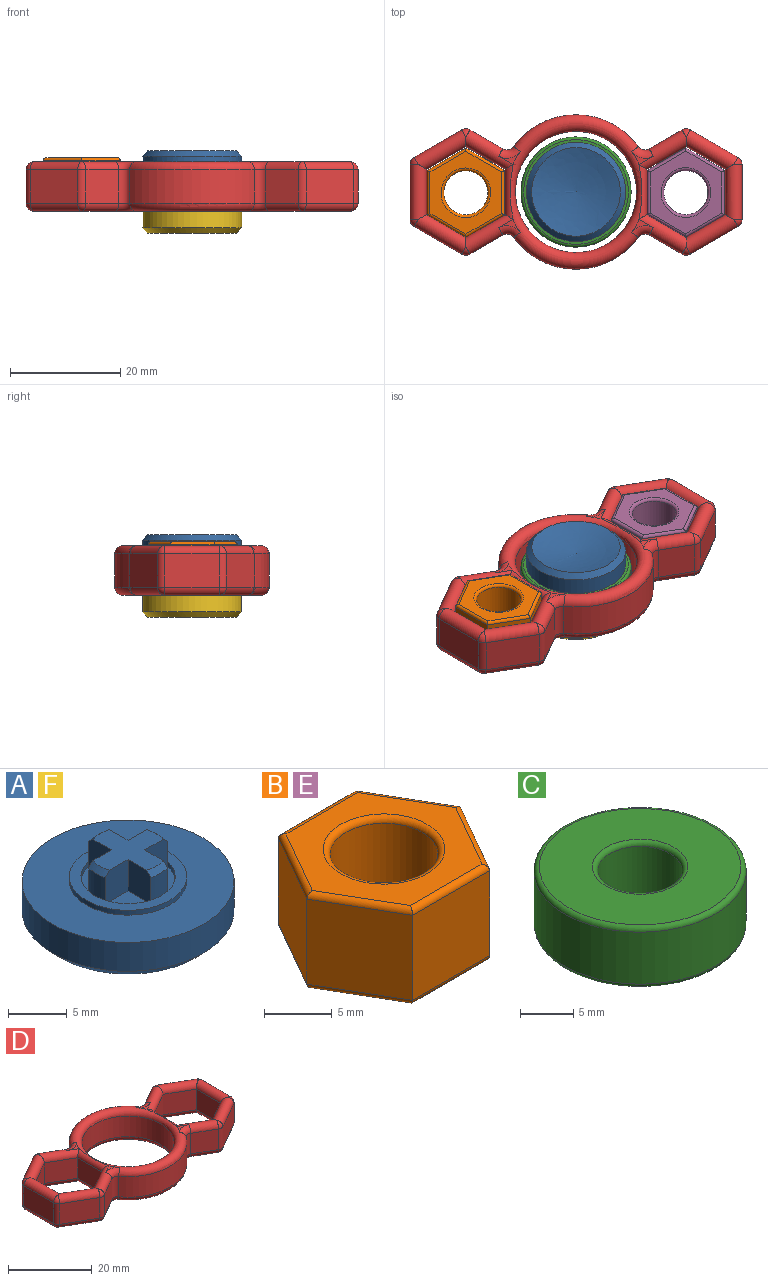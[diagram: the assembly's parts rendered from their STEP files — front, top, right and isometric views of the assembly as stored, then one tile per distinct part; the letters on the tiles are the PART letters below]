
ASSEMBLY  parts=6 mates=5
PART A: 25 faces, bbox 18x18x7.2 mm
  f0: cone r=9mm half-angle=45deg, axis (0,0,1), area 72.9mm2, adj f1,f3
  f1: cylinder r=9mm len=18mm, axis (0,0,-1), area 169.6mm2, adj f0,f2
  f2: plane 18x18mm, normal (0,0,1), area 176.5mm2, adj f1,f5
  f3: revolved ~0x0mm, area 0mm2, adj f0
  f4: cylinder r=4mm len=8mm, axis (0,0,-1), area 12.6mm2, adj f6,f24
  f5: cylinder r=4.98mm len=9.96mm, axis (0,0,-1), area 15.7mm2, adj f2,f6
  f6: plane 9.96x9.96mm, normal (0,0,1), area 27.7mm2, adj f4,f5
  f7: cone r=3.38mm half-angle=45deg, axis (0,0,-1), area 1.4mm2, adj f10,f13,f14,f15
  f8: cone r=3.38mm half-angle=45deg, axis (0,0,-1), area 1.4mm2, adj f10,f16,f17,f18
  f9: cone r=3.38mm half-angle=45deg, axis (0,0,-1), area 1.4mm2, adj f10,f19,f20,f21
  f10: plane 6.75x6.75mm, normal (0,0,1), area 22.6mm2, adj f7,f8,f9,f11,f12,f13,f15,f16
  f11: cone r=3.38mm half-angle=45deg, axis (0,0,-1), area 1.4mm2, adj f10,f12,f22,f23
  f12: plane 3.26x2.75mm, normal (-1,0,0), area 8.8mm2, adj f10,f11,f13,f23,f24
  f13: plane 3.26x2.75mm, normal (0,1,0), area 8.8mm2, adj f7,f10,f12,f14,f24
  f14: cylinder r=3.88mm len=2.75mm, axis (0,0,-1), area 5.6mm2, adj f7,f13,f15,f24
  f15: plane 3.26x2.75mm, normal (0,-1,0), area 8.8mm2, adj f7,f10,f14,f16,f24
  f16: plane 3.26x2.75mm, normal (-1,0,0), area 8.8mm2, adj f8,f10,f15,f17,f24
  f17: cylinder r=3.88mm len=2.75mm, axis (0,0,-1), area 5.6mm2, adj f8,f16,f18,f24
  f18: plane 3.26x2.75mm, normal (1,0,0), area 8.8mm2, adj f8,f10,f17,f19,f24
  f19: plane 3.26x2.75mm, normal (0,-1,0), area 8.8mm2, adj f9,f10,f18,f20,f24
  f20: cylinder r=3.88mm len=2.75mm, axis (0,0,-1), area 5.6mm2, adj f9,f19,f21,f24
  f21: plane 3.26x2.75mm, normal (0,1,0), area 8.8mm2, adj f9,f10,f20,f22,f24
  f22: plane 3.26x2.75mm, normal (1,0,0), area 8.8mm2, adj f10,f11,f21,f23,f24
  f23: cylinder r=3.88mm len=2.75mm, axis (0,0,-1), area 5.6mm2, adj f11,f12,f22,f24
  f24: plane 8x8mm, normal (0,0,1), area 23.6mm2, adj f4,f12,f13,f14,f15,f16,f17,f18
PART B: 23 faces, bbox 16.2x14x8.7 mm
  f0: plane 7.7x6.99mm, normal (0.86,0.5,0), area 62.2mm2, adj f1,f6,f11,f18
  f1: plane 8.08x7.7mm, normal (0,1,0), area 62.2mm2, adj f0,f2,f10,f17
  f2: plane 7.7x7.01mm, normal (-0.87,0.5,0), area 62.2mm2, adj f1,f3,f12,f19
  f3: plane 7.7x6.99mm, normal (-0.86,-0.5,0), area 62.2mm2, adj f2,f4,f14,f21
  f4: plane 8.08x7.7mm, normal (0,-1,0), area 62.2mm2, adj f3,f6,f15,f22
  f5: cylinder r=4mm len=8mm, axis (0,0,-1), area 193.5mm2, adj f9,f16
  f6: plane 7.7x7.01mm, normal (0.87,-0.5,0), area 62.2mm2, adj f0,f4,f13,f20
  f7: plane 15.01x13.02mm, normal (0,0,1), area 82.7mm2, adj f16,f17,f18,f19,f20,f21,f22
  f8: plane 15.01x13.02mm, normal (0,0,-1), area 82.7mm2, adj f9,f10,f11,f12,f13,f14,f15
  f9: torus R=4.5mm, axis (0,0,1), area 20.6mm2, adj f5,f8
  f10: cylinder r=0.5mm len=8.08mm, axis (-1,0,0), area 6.2mm2, adj f1,f8,f11,f12
  f11: cylinder r=0.5mm len=7.24mm, axis (-0.5,0.86,0), area 6.2mm2, adj f0,f8,f10,f13
  f12: cylinder r=0.5mm len=7.26mm, axis (-0.5,-0.87,0), area 6.2mm2, adj f2,f8,f10,f14
  f13: cylinder r=0.5mm len=7.26mm, axis (0.5,0.87,0), area 6.2mm2, adj f6,f8,f11,f15
  f14: cylinder r=0.5mm len=7.24mm, axis (0.5,-0.86,0), area 6.2mm2, adj f3,f8,f12,f15
  f15: cylinder r=0.5mm len=8.08mm, axis (1,0,0), area 6.2mm2, adj f4,f8,f13,f14
  f16: torus R=4.5mm, axis (0,0,1), area 20.6mm2, adj f5,f7
  f17: cylinder r=0.5mm len=8.08mm, axis (1,0,0), area 6.2mm2, adj f1,f7,f18,f19
  f18: cylinder r=0.5mm len=7.24mm, axis (0.5,-0.86,0), area 6.2mm2, adj f0,f7,f17,f20
  f19: cylinder r=0.5mm len=7.26mm, axis (0.5,0.87,0), area 6.2mm2, adj f2,f7,f17,f21
  f20: cylinder r=0.5mm len=7.26mm, axis (-0.5,-0.87,0), area 6.2mm2, adj f6,f7,f18,f22
  f21: cylinder r=0.5mm len=7.24mm, axis (-0.5,0.86,0), area 6.2mm2, adj f3,f7,f19,f22
  f22: cylinder r=0.5mm len=8.08mm, axis (-1,0,0), area 6.2mm2, adj f4,f7,f20,f21
PART C: 8 faces, bbox 21.6x21.6x7 mm
  f0: cylinder r=4mm len=8mm, axis (0,0,-1), area 150.8mm2, adj f4,f6
  f1: cylinder r=10mm len=20mm, axis (0,0,-1), area 377mm2, adj f5,f7
  f2: plane 19x19mm, normal (0,0,1), area 219.9mm2, adj f6,f7
  f3: plane 19x19mm, normal (0,0,-1), area 219.9mm2, adj f4,f5
  f4: torus R=4.5mm, axis (0,0,1), area 20.6mm2, adj f0,f3
  f5: torus R=9.5mm, axis (0,0,1), area 48.5mm2, adj f1,f3
  f6: torus R=4.5mm, axis (0,0,1), area 20.6mm2, adj f0,f2
  f7: torus R=9.5mm, axis (0,0,1), area 48.5mm2, adj f1,f2
PART D: 95 faces, bbox 60.3x30.3x9 mm
  f0: plane 3.93x2.33mm, normal (0,0,1), area 1.8mm2, adj f71,f86,f87
  f1: plane 3.93x2.33mm, normal (0,0,1), area 1.8mm2, adj f57,f58,f71
  f2: plane 3.93x2.33mm, normal (0,0,1), area 1.8mm2, adj f59,f60,f71
  f3: plane 3.93x2.33mm, normal (0,0,-1), area 1.8mm2, adj f76,f88,f89
  f4: plane 3.93x2.33mm, normal (0,0,-1), area 1.8mm2, adj f66,f67,f76
  f5: plane 3.93x2.33mm, normal (0,0,-1), area 1.8mm2, adj f64,f65,f76
  f6: plane 8.63x6mm, normal (-0.5,-0.87,0), area 59.8mm2, adj f83,f85,f90,f94
  f7: plane 6x5.96mm, normal (0.5,-0.87,0), area 41.3mm2, adj f80,f86,f89,f94
  f8: cylinder r=14mm len=22.65mm, axis (0,0,-1), area 158.3mm2, adj f62,f71,f76,f80
  f9: plane 6x5.96mm, normal (-0.5,-0.87,0), area 41.3mm2, adj f38,f61,f62,f63
  f10: plane 8.63x6mm, normal (0.5,-0.87,0), area 59.8mm2, adj f33,f38,f46,f49
  f11: plane 9.96x6mm, normal (1,0,0), area 59.8mm2, adj f33,f34,f36,f40
  f12: plane 8.63x6mm, normal (0.5,0.87,0), area 59.8mm2, adj f34,f43,f45,f50
  f13: plane 6x5.96mm, normal (-0.5,0.87,0), area 41.3mm2, adj f43,f52,f60,f64
  f14: cylinder r=14mm len=22.65mm, axis (0,0,-1), area 158.3mm2, adj f52,f54,f71,f76
  f15: plane 6x5.96mm, normal (0.5,0.87,0), area 41.3mm2, adj f42,f54,f57,f67
  f16: plane 8.63x6mm, normal (-0.5,0.87,0), area 59.8mm2, adj f42,f56,f68,f69
  f17: plane 8.23x6mm, normal (1,0,0), area 49.4mm2, adj f18,f27,f78,f82
  f18: plane 7.13x6mm, normal (0.5,-0.87,0), area 49.4mm2, adj f17,f19,f56,f68
  f19: plane 7.13x6mm, normal (-0.5,-0.87,0), area 49.4mm2, adj f18,f20,f57,f67
  f20: plane 8.23x6mm, normal (-1,0,0), area 49.4mm2, adj f19,f21,f79,f81
  f21: plane 7.13x6mm, normal (-0.5,0.87,0), area 49.4mm2, adj f20,f27,f86,f89
  f22: plane 7.13x6mm, normal (-0.5,0.87,0), area 49.4mm2, adj f23,f28,f46,f49
  f23: plane 7.13x6mm, normal (0.5,0.87,0), area 49.4mm2, adj f22,f24,f61,f63
  f24: plane 8.23x6mm, normal (1,0,0), area 49.4mm2, adj f23,f25,f72,f75
  f25: plane 7.13x6mm, normal (0.5,-0.87,0), area 49.4mm2, adj f24,f26,f60,f64
  f26: plane 7.13x6mm, normal (-0.5,-0.87,0), area 49.4mm2, adj f25,f28,f45,f50
  f27: plane 7.13x6mm, normal (0.5,0.87,0), area 49.4mm2, adj f17,f21,f85,f90
  f28: plane 8.23x6mm, normal (-1,0,0), area 49.4mm2, adj f22,f26,f36,f40
  f29: cylinder r=11mm len=22mm, axis (0,0,-1), area 414.7mm2, adj f71,f76
  f30: plane 9.96x6mm, normal (-1,0,0), area 59.8mm2, adj f69,f78,f82,f83
  f31: plane 3.93x2.33mm, normal (0,0,1), area 1.8mm2, adj f61,f71,f73
  f32: plane 3.93x2.33mm, normal (0,0,-1), area 1.8mm2, adj f63,f74,f76
  f33: cylinder r=1.5mm len=6mm, axis (0,0,-1), area 9.4mm2, adj f10,f11,f37,f39
  f34: cylinder r=1.5mm len=6mm, axis (0,0,-1), area 9.4mm2, adj f11,f12,f35,f41
  f35: sphere r=1.5mm, area 2.4mm2, adj f34,f36,f45
  f36: cylinder r=1.5mm len=9.96mm, axis (0,-1,0), area 44.3mm2, adj f11,f28,f35,f37,f45,f46
  f37: sphere r=1.5mm, area 2.4mm2, adj f33,f36,f46
  f38: cylinder r=1.5mm len=6mm, axis (0,0,-1), area 9.4mm2, adj f9,f10,f47,f48
  f39: sphere r=1.5mm, area 2.4mm2, adj f33,f40,f49
  f40: cylinder r=1.5mm len=9.96mm, axis (0,1,0), area 44.3mm2, adj f11,f28,f39,f41,f49,f50
  f41: sphere r=1.5mm, area 2.4mm2, adj f34,f40,f50
  f42: cylinder r=1.5mm len=6mm, axis (0,0,-1), area 9.4mm2, adj f15,f16,f53,f55
  f43: cylinder r=1.5mm len=6mm, axis (0,0,-1), area 9.4mm2, adj f12,f13,f44,f51
  f44: sphere r=1.5mm, area 2.4mm2, adj f43,f45,f60
  f45: cylinder r=1.5mm len=10.13mm, axis (0.87,-0.5,0), area 44.3mm2, adj f12,f26,f35,f36,f44,f60
  f46: cylinder r=1.5mm len=10.13mm, axis (-0.87,-0.5,0), area 44.3mm2, adj f10,f22,f36,f37,f47,f61
  f47: sphere r=1.5mm, area 2.4mm2, adj f38,f46,f61
  f48: sphere r=1.5mm, area 2.4mm2, adj f38,f49,f63
  f49: cylinder r=1.5mm len=10.13mm, axis (0.87,0.5,0), area 44.3mm2, adj f10,f22,f39,f40,f48,f63
  f50: cylinder r=1.5mm len=10.13mm, axis (-0.87,0.5,0), area 44.3mm2, adj f12,f26,f40,f41,f51,f64
  f51: sphere r=1.5mm, area 2.4mm2, adj f43,f50,f64
  f52: cylinder r=1.5mm len=6mm, axis (0,0,-1), area 13.2mm2, adj f13,f14,f59,f65
  f53: sphere r=1.5mm, area 2.4mm2, adj f42,f56,f57
  f54: cylinder r=1.5mm len=6mm, axis (0,0,-1), area 13.2mm2, adj f14,f15,f58,f66
  f55: sphere r=1.5mm, area 2.4mm2, adj f42,f67,f68
  f56: cylinder r=1.5mm len=10.13mm, axis (0.87,0.5,0), area 44.3mm2, adj f16,f18,f53,f57,f70,f78
  f57: cylinder r=1.5mm len=10.1mm, axis (0.87,-0.5,0), area 37.1mm2, adj f1,f15,f19,f53,f56,f58,f71,f79
  f58: torus R=3mm, axis (0,0,1), area 7.1mm2, adj f1,f54,f57,f71
  f59: torus R=3mm, axis (0,0,1), area 7.1mm2, adj f2,f52,f60,f71
  f60: cylinder r=1.5mm len=10.1mm, axis (0.87,0.5,0), area 37.1mm2, adj f2,f13,f25,f44,f45,f59,f71,f72
  f61: cylinder r=1.5mm len=10.1mm, axis (-0.87,0.5,0), area 37.1mm2, adj f9,f23,f31,f46,f47,f71,f72,f73
  f62: cylinder r=1.5mm len=6mm, axis (0,0,-1), area 13.2mm2, adj f8,f9,f73,f74
  f63: cylinder r=1.5mm len=10.1mm, axis (0.87,-0.5,0), area 37.1mm2, adj f9,f23,f32,f48,f49,f74,f75,f76
  f64: cylinder r=1.5mm len=10.1mm, axis (-0.87,-0.5,0), area 37.1mm2, adj f5,f13,f25,f50,f51,f65,f75,f76
  f65: torus R=3mm, axis (0,0,1), area 7.1mm2, adj f5,f52,f64,f76
  f66: torus R=3mm, axis (0,0,1), area 7.1mm2, adj f4,f54,f67,f76
  f67: cylinder r=1.5mm len=10.1mm, axis (-0.87,0.5,0), area 37.1mm2, adj f4,f15,f19,f55,f66,f68,f76,f81
  f68: cylinder r=1.5mm len=10.13mm, axis (-0.87,-0.5,0), area 44.3mm2, adj f16,f18,f55,f67,f77,f82
  f69: cylinder r=1.5mm len=6mm, axis (0,0,-1), area 9.4mm2, adj f16,f30,f70,f77
  f70: sphere r=1.5mm, area 2.4mm2, adj f56,f69,f78
  f71: torus R=12.5mm, axis (0,0,1), area 282.4mm2, adj f0,f1,f2,f8,f14,f29,f31,f57
  f72: cylinder r=1.5mm len=9.9mm, axis (0,-1,0), area 16.9mm2, adj f24,f60,f61,f71
  f73: torus R=3mm, axis (0,0,1), area 7.1mm2, adj f31,f61,f62,f71
  f74: torus R=3mm, axis (0,0,1), area 7.1mm2, adj f32,f62,f63,f76
  f75: cylinder r=1.5mm len=9.9mm, axis (0,1,0), area 16.9mm2, adj f24,f63,f64,f76
  f76: torus R=12.5mm, axis (0,0,1), area 282.4mm2, adj f3,f4,f5,f8,f14,f29,f32,f63
  f77: sphere r=1.5mm, area 2.4mm2, adj f68,f69,f82
  f78: cylinder r=1.5mm len=9.96mm, axis (0,1,0), area 44.3mm2, adj f17,f30,f56,f70,f84,f85
  f79: cylinder r=1.5mm len=9.9mm, axis (0,1,0), area 16.9mm2, adj f20,f57,f71,f86
  f80: cylinder r=1.5mm len=6mm, axis (0,0,-1), area 13.2mm2, adj f7,f8,f87,f88
  f81: cylinder r=1.5mm len=9.9mm, axis (0,-1,0), area 16.9mm2, adj f20,f67,f76,f89
  f82: cylinder r=1.5mm len=9.96mm, axis (0,1,0), area 44.3mm2, adj f17,f30,f68,f77,f90,f91
  f83: cylinder r=1.5mm len=6mm, axis (0,0,-1), area 9.4mm2, adj f6,f30,f84,f91
  f84: sphere r=1.5mm, area 2.4mm2, adj f78,f83,f85
  f85: cylinder r=1.5mm len=10.13mm, axis (0.87,-0.5,0), area 44.3mm2, adj f6,f27,f78,f84,f86,f92
  f86: cylinder r=1.5mm len=10.1mm, axis (0.87,0.5,0), area 37.1mm2, adj f0,f7,f21,f71,f79,f85,f87,f92
  f87: torus R=3mm, axis (0,0,1), area 7.1mm2, adj f0,f71,f80,f86
  f88: torus R=3mm, axis (0,0,1), area 7.1mm2, adj f3,f76,f80,f89
  f89: cylinder r=1.5mm len=10.1mm, axis (-0.87,-0.5,0), area 37.1mm2, adj f3,f7,f21,f76,f81,f88,f90,f93
  f90: cylinder r=1.5mm len=10.13mm, axis (-0.87,0.5,0), area 44.3mm2, adj f6,f27,f82,f89,f91,f93
  f91: sphere r=1.5mm, area 2.4mm2, adj f82,f83,f90
  f92: sphere r=1.5mm, area 2.4mm2, adj f85,f86,f94
  f93: sphere r=1.5mm, area 2.4mm2, adj f89,f90,f94
  f94: cylinder r=1.5mm len=6mm, axis (0,0,-1), area 9.4mm2, adj f6,f7,f92,f93
PART E: same geometry as B
PART F: same geometry as A
PLACE A rot(axis=(1,0,0),180deg) t=(-33.06,11.01,-0.49)mm
PLACE B rot(axis=(0,0,-1),150.1deg) t=(-53.06,10.87,-10.49)mm
PLACE C t=(-33.06,11.01,-11.49)mm
PLACE D t=(-33.06,11.01,-11.49)mm
PLACE E rot(axis=(0,0,1),89.9deg) t=(-13.12,10.91,-11.34)mm
PLACE F t=(-33.06,11.01,-15.49)mm
MATE fastened E.f2 <-> D.f23  axis (-0.5,-0.87,0) through (-16.62,4.84,-6.99)mm
MATE fastened F.f0 <-> C.f0  axis (0,0,1) through (-33.06,11.01,-11.49)mm
MATE fastened B.f1 <-> D.f21  axis (0.5,-0.87,0) through (-53.06,2.79,-9.99)mm
MATE fastened C.f0 <-> D.f8  axis (0,0,1) through (-33.06,11.01,-4.49)mm
MATE fastened A.f0 <-> C.f0  axis (0,0,-1) through (-33.06,11.01,-4.49)mm
